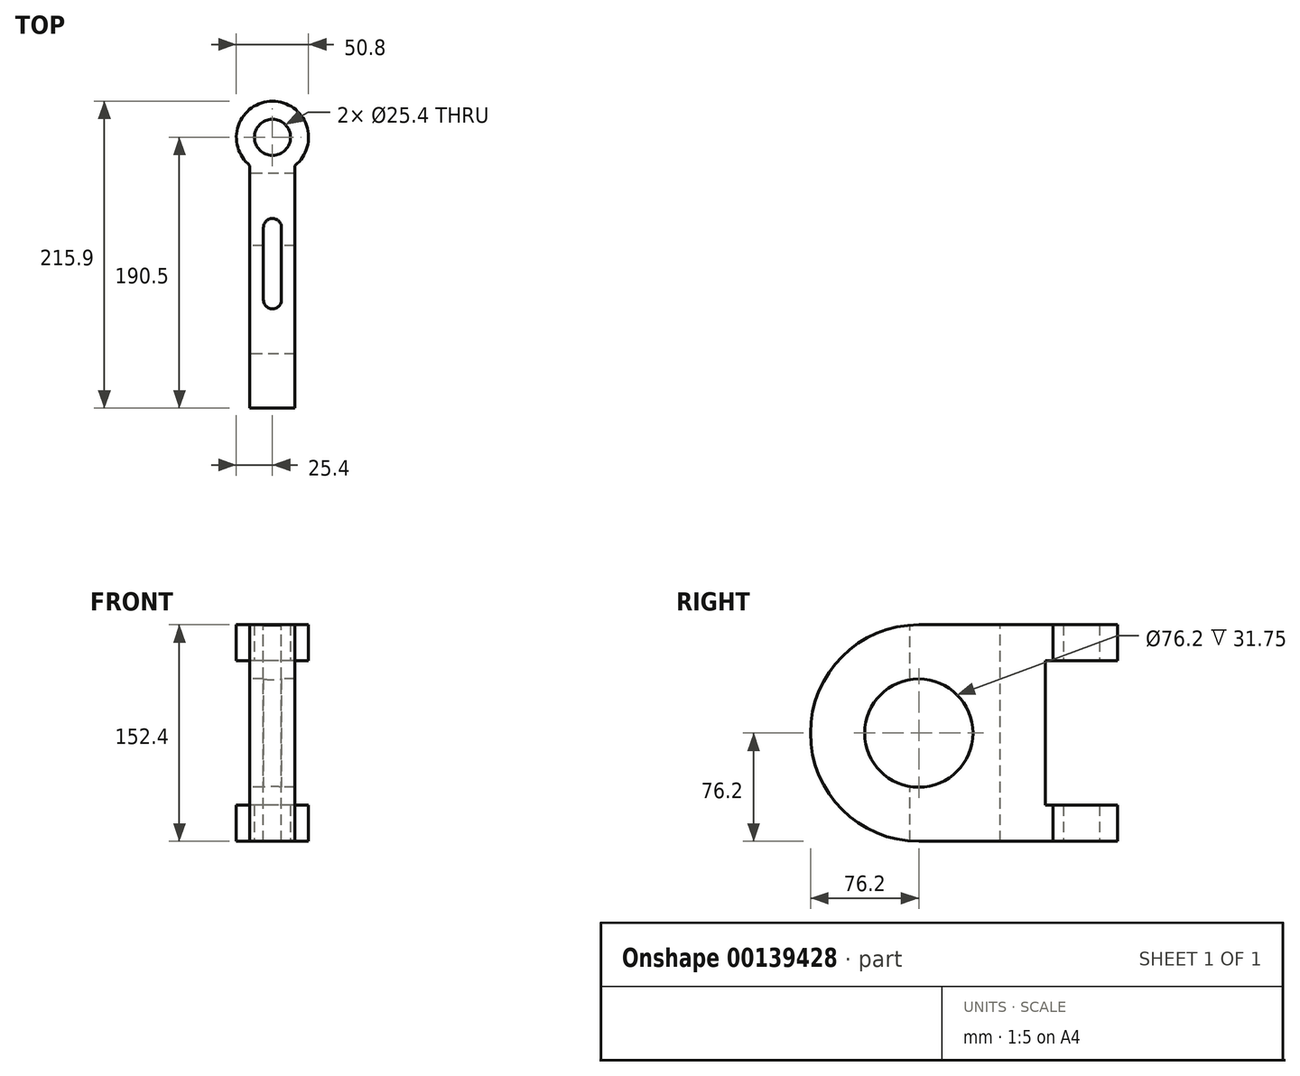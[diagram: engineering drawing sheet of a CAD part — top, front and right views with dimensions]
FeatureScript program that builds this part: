
annotation { "Feature Type Name" : "Feature", "Feature Type Description" : "" }
export const myFeature = defineFeature(function(context is Context, id is Id, definition is map)
    precondition{}
    {
        {
            var Q0;
            Q0=qCreatedBy(makeId("Top.planeOp"),FACE);
            var sketch = newSketch(context, id + "F0", { "sketchPlane" : qUnion([Q0])});
            skCircle(sketch, "E0", {"center": v(0, 0) * mm, "radius": 12.7 * mm});
            skArc(sketch, "E1", {"start": v(15.88, -19.83) * mm, "mid": v(0, 25.4) * mm, "end": v(-15.88, -19.83) * mm});
            skLineSegment(sketch, "E2", {"start": v(-15.88, -19.83) * mm, "end": v(-15.87, -190.5) * mm});
            skLineSegment(sketch, "E3", {"start": v(15.87, -19.83) * mm, "end": v(15.88, -190.5) * mm});
            skLineSegment(sketch, "E4", {"start": v(-15.87, -190.5) * mm, "end": v(15.87, -190.5) * mm});
            skSolve(sketch);
        }
        {
            var Q0;
            Q0 = qSketchRegion(id + "F0", true);
            extrude(context, id + "F1", {"entities" : qUnion([Q0]), "depth" : 152.4 * mm});
        }
        {
            var Q0;
            Q0=makeQuery(id+"F1.opExtrude","CAP_EDGE",EDGE,{"disambiguationData":[OSD([sQuery(id+"F0.wireOp",EDGE,"E4")])],"isStart":false});
            var Q1;
            Q1=makeQuery(id+"F1.opExtrude","CAP_EDGE",EDGE,{"disambiguationData":[OSD([sQuery(id+"F0.wireOp",EDGE,"E4")])],"isStart":true});
            fillet(context, id + "F2", {"entities" : qUnion([Q0, Q1]), "radius" : 76.2 * mm, "tangentPropagation" : true, "allowEdgeOverflow" : false});
        }
        {
            var Q0;
            Q0=makeQuery(id+"F1.opExtrude","SWEPT_FACE",FACE,{"disambiguationData":[OSD([sQuery(id+"F0.wireOp",EDGE,"E2")])]});
            var sketch = newSketch(context, id + "F3", { "sketchPlane" : qUnion([Q0])});
            skCircle(sketch, "E5", {"center": v(114.3, 76.2) * mm, "radius": 38.1 * mm});
            skPoint(sketch, "E6.orphan", {"position": v(114.3, 152.4) * mm});
            skPoint(sketch, "E7.end.orphan", {"position": v(114.3, 0) * mm});
            skLineSegment(sketch, "E8.bottom", {"start": v(25.4, 25.4) * mm, "end": v(-58.73, 25.4) * mm});
            skLineSegment(sketch, "E8.top", {"start": v(25.4, 127) * mm, "end": v(-58.73, 127) * mm});
            skLineSegment(sketch, "E8.left", {"start": v(25.4, 25.4) * mm, "end": v(25.4, 127) * mm});
            skLineSegment(sketch, "E8.right", {"start": v(-58.73, 25.4) * mm, "end": v(-58.73, 127) * mm});
            skSolve(sketch);
        }
        {
            var Q0;
            Q0 = qSketchRegion(id + "F3", true);
            extrude(context, id + "F4", {"entities" : qUnion([Q0]), "operationType" : NewBodyOperationType.REMOVE, "endBound" : BoundingType.SYMMETRIC, "oppositeDirection" : true, "depth" : 12700 * mm});
        }
        {
            var Q0;
            Q0=makeQuery(id+"F1.opExtrude","CAP_FACE",FACE,{"disambiguationData":[OSD([sQuery(id+"F0.wireOp",EDGE,"E0"),sQuery(id+"F0.wireOp",EDGE,"E1"),sQuery(id+"F0.wireOp",EDGE,"E2"),sQuery(id+"F0.wireOp",EDGE,"E3"),sQuery(id+"F0.wireOp",EDGE,"E4")])],"isStart":false});
            var sketch = newSketch(context, id + "F5", { "sketchPlane" : qUnion([Q0])});
            skCircle(sketch, "E9.0", {"center": v(0, 0) * mm, "radius": 12.7 * mm});
            skLineSegment(sketch, "E10", {"start": v(-6.35, -63.5) * mm, "end": v(-6.35, -114.3) * mm});
            skLineSegment(sketch, "E11", {"start": v(6.35, -63.5) * mm, "end": v(6.35, -114.3) * mm});
            skArc(sketch, "E12", {"start": v(-6.35, -114.3) * mm, "mid": v(0, -120.65) * mm, "end": v(6.35, -114.3) * mm});
            skArc(sketch, "E13", {"start": v(6.35, -63.5) * mm, "mid": v(0, -57.15) * mm, "end": v(-6.35, -63.5) * mm});
            skSolve(sketch);
        }
        {
            var Q0;
            Q0=makeQuery(id+"F5.imprint","IMPRINT",FACE,{"disambiguationData":[TD([[makeQuery(id+"F5.imprint","IMPRINT",EDGE,{"derivedFrom":sQuery(id+"F5.wireOp",EDGE,"E10")}),1.0]])]});
            extrude(context, id + "F6", {"entities" : qUnion([Q0]), "operationType" : NewBodyOperationType.REMOVE, "endBound" : BoundingType.SYMMETRIC, "oppositeDirection" : true, "depth" : 483.24 * mm});
        }
        {
            var Q0;
            Q0 = qSketchRegion(id + "F5", true);
            extrude(context, id + "F7", {"entities" : qUnion([Q0]), "operationType" : NewBodyOperationType.REMOVE, "oppositeDirection" : true, "depth" : 170.2 * mm});
        }
    });
